# Revit family: Mixer-Basin-Dorf Enigma-Wall
name_source: partatom
category: Plumbing Fixtures
revit_build: Autodesk Revit 2014 (Build: 20131024_2115(x64)
units: mm (PartAtom-declared; Revit-internal decimal feet)

## types (1)
- Standard
    Assembly Code = D2020300
    CW Connection = Yes
    CWFU = 1.58
    Connector Radius = 10 mm  [stored 0.0328084 ft]
    Cost = 0 $
    Default Elevation = 1100 mm
    HW Connection = Yes
    HWFU = 1.58
    Height_ANZRS = 80 mm  [stored 0.262467 ft]
    Length_ANZRS = 180 mm  [stored 0.590551 ft]
    Manufacturer = GWA Bathrooms & Kitchens
    Material_ANZRS = Metal-Chrome-Caroma
    Model = 6484.045A
    ModifiedIssue_ANZRS = 20150428 $
    Type Comments = Dorf Enigma Wall Basin/Bath Mixer
    URL = http://specify.caroma.com.au
    Vent Connection = No
    WELSRating_ANZRS = WELS 5 star rated, 6L/min
    Waste Connection = No
    Width_ANZRS = 224 mm

note: [stored X ft] marks values corroborated as IEEE doubles in the binary element streams (Revit-internal decimal feet)

## geometry (parser evidence)
native form markers: Blend x10, Sweep x1
no freeform markers — native parametric forms only
